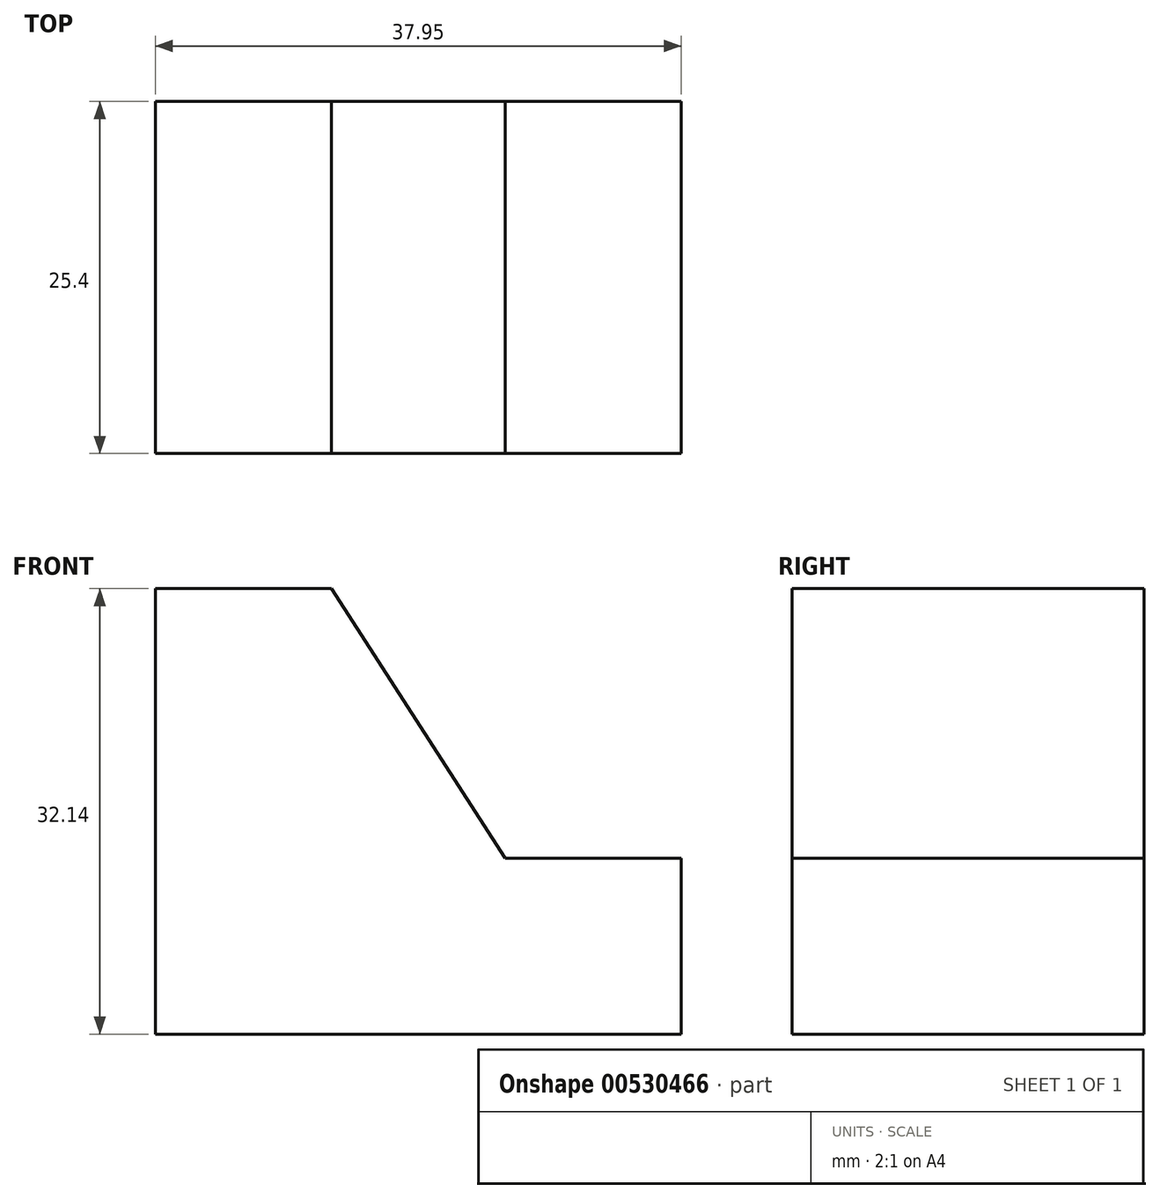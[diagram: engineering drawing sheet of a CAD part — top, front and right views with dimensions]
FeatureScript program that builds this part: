
annotation { "Feature Type Name" : "Feature", "Feature Type Description" : "" }
export const myFeature = defineFeature(function(context is Context, id is Id, definition is map)
    precondition{}
    {
        {
            var Q0;
            Q0=qCreatedBy(makeId("Front.planeOp"),FACE);
            var sketch = newSketch(context, id + "F0", { "sketchPlane" : qUnion([Q0])});
            skLineSegment(sketch, "E0", {"start": v(-47.87, 0) * mm, "end": v(-47.87, 32.14) * mm});
            skLineSegment(sketch, "E1", {"start": v(-47.87, 32.14) * mm, "end": v(-9.92, 32.14) * mm});
            skLineSegment(sketch, "E2", {"start": v(-9.92, 32.14) * mm, "end": v(-9.92, 0) * mm});
            skLineSegment(sketch, "E3", {"start": v(-9.92, 0) * mm, "end": v(-47.87, 0) * mm});
            skSolve(sketch);
        }
        {
            var Q0;
            Q0=makeQuery(id+"F0.imprint","IMPRINT",FACE,{"disambiguationData":[TD([[makeQuery(id+"F0.imprint","IMPRINT",EDGE,{"derivedFrom":sQuery(id+"F0.wireOp",EDGE,"E0")}),-1.0]])]});
            extrude(context, id + "F1", {"entities" : qUnion([Q0]), "depth" : 25.4 * mm, "offsetDistance" : 25.4 * mm});
        }
        {
            var Q0;
            Q0=makeQuery(id+"F1.opExtrude","CAP_FACE",FACE,{"disambiguationData":[OSD([sQuery(id+"F0.wireOp",EDGE,"E0"),sQuery(id+"F0.wireOp",EDGE,"E1"),sQuery(id+"F0.wireOp",EDGE,"E2"),sQuery(id+"F0.wireOp",EDGE,"E3")])],"isStart":false});
            var sketch = newSketch(context, id + "F2", { "sketchPlane" : qUnion([Q0])});
            skLineSegment(sketch, "E4", {"start": v(-35.17, 32.14) * mm, "end": v(-22.62, 12.7) * mm});
            skLineSegment(sketch, "E5", {"start": v(-22.62, 12.7) * mm, "end": v(-9.92, 12.7) * mm});
            skSolve(sketch);
        }
        {
            var Q0;
            {var subQ0=sQuery(id+"F2.wireOp",EDGE,"E4");Q0=makeQuery(id+"F2.imprint","IMPRINT",FACE,{"disambiguationData":[TD([[makeQuery(id+"F2.imprint","IMPRINT",EDGE,{"derivedFrom":subQ0}),1.0]])]});}
            extrude(context, id + "F3", {"entities" : qUnion([Q0]), "operationType" : NewBodyOperationType.REMOVE, "endBound" : BoundingType.THROUGH_ALL, "oppositeDirection" : true, "depth" : 25.4 * mm, "offsetDistance" : 25.4 * mm});
        }
    });
